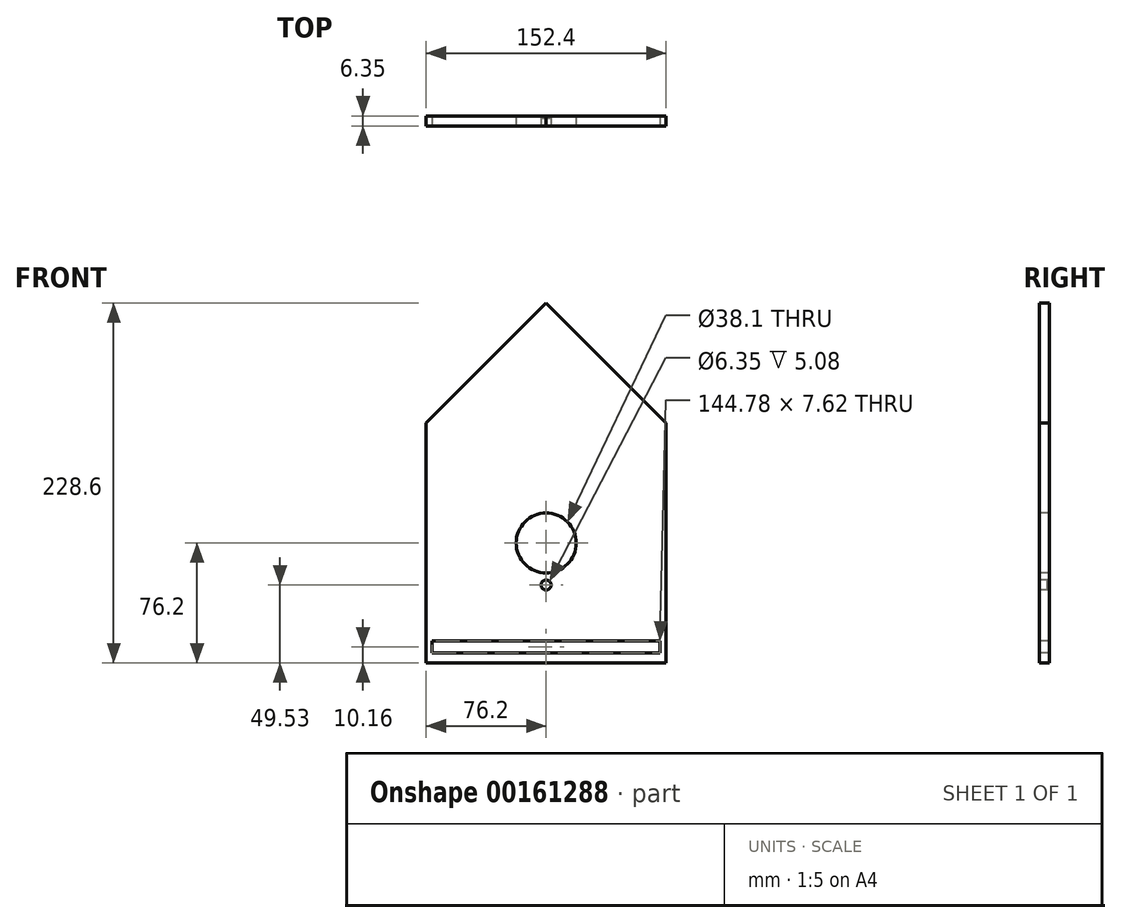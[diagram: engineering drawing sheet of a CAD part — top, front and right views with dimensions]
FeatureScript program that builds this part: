
annotation { "Feature Type Name" : "Feature", "Feature Type Description" : "" }
export const myFeature = defineFeature(function(context is Context, id is Id, definition is map)
    precondition{}
    {
        {
            var Q0;
            Q0=qCreatedBy(makeId("Front.planeOp"),FACE);
            var sketch = newSketch(context, id + "F0", { "sketchPlane" : qUnion([Q0])});
            skLineSegment(sketch, "E0.bottom", {"start": v(0, 0) * mm, "end": v(152.4, 0) * mm});
            skLineSegment(sketch, "E0.top", {"start": v(0, -152.4) * mm, "end": v(152.4, -152.4) * mm});
            skLineSegment(sketch, "E0.left", {"start": v(0, 0) * mm, "end": v(0, -152.4) * mm});
            skLineSegment(sketch, "E0.right", {"start": v(152.4, 0) * mm, "end": v(152.4, -152.4) * mm});
            skLineSegment(sketch, "E1", {"start": v(0, 0) * mm, "end": v(76.2, 76.2) * mm});
            skLineSegment(sketch, "E2", {"start": v(76.2, 76.2) * mm, "end": v(152.4, 0) * mm});
            skSolve(sketch);
        }
        {
            var Q0;
            Q0 = qSketchRegion(id + "F0", true);
            extrude(context, id + "F1", {"entities" : qUnion([Q0]), "depth" : 6.35 * mm});
        }
        {
            var Q0;
            Q0=makeQuery(id+"F1.opExtrude","CAP_FACE",FACE,{"disambiguationData":[OSD([sQuery(id+"F0.wireOp",EDGE,"E0.top"),sQuery(id+"F0.wireOp",EDGE,"E0.left"),sQuery(id+"F0.wireOp",EDGE,"E0.right"),sQuery(id+"F0.wireOp",EDGE,"E1"),sQuery(id+"F0.wireOp",EDGE,"E2")])],"isStart":false});
            var sketch = newSketch(context, id + "F2", { "sketchPlane" : qUnion([Q0])});
            skLineSegment(sketch, "E3", {"start": v(0, 0) * mm, "end": v(152.4, -152.4) * mm, "construction": true});
            skLineSegment(sketch, "E4", {"start": v(0, -152.4) * mm, "end": v(152.4, 0) * mm, "construction": true});
            skCircle(sketch, "E5", {"center": v(76.2, -76.2) * mm, "radius": 19.05 * mm});
            skSolve(sketch);
        }
        {
            var Q0;
            Q0=makeQuery(id+"F2.imprint","IMPRINT",FACE,{"disambiguationData":[TD([[makeQuery(id+"F2.imprint","IMPRINT",EDGE,{"derivedFrom":sQuery(id+"F2.wireOp",EDGE,"E5")}),1.0]])]});
            extrude(context, id + "F3", {"entities" : qUnion([Q0]), "operationType" : NewBodyOperationType.REMOVE, "endBound" : BoundingType.THROUGH_ALL, "oppositeDirection" : true, "depth" : 6.6 * mm});
        }
        {
            var Q0;
            Q0=makeQuery(id+"F1.opExtrude","CAP_FACE",FACE,{"disambiguationData":[OSD([sQuery(id+"F0.wireOp",EDGE,"E0.top"),sQuery(id+"F0.wireOp",EDGE,"E0.left"),sQuery(id+"F0.wireOp",EDGE,"E0.right"),sQuery(id+"F0.wireOp",EDGE,"E1"),sQuery(id+"F0.wireOp",EDGE,"E2")])],"isStart":false});
            var sketch = newSketch(context, id + "F4", { "sketchPlane" : qUnion([Q0])});
            skCircle(sketch, "E6", {"center": v(76.2, -102.87) * mm, "radius": 3.18 * mm});
            skPoint(sketch, "E6.centerSnap0", {"position": v(76.2, -152.4) * mm});
            skSolve(sketch);
        }
        {
            var Q0;
            Q0 = qSketchRegion(id + "F4", true);
            extrude(context, id + "F5", {"entities" : qUnion([Q0]), "operationType" : NewBodyOperationType.REMOVE, "oppositeDirection" : true, "depth" : 5.08 * mm});
        }
        {
            var Q0;
            Q0=makeQuery(id+"F1.opExtrude","CAP_FACE",FACE,{"disambiguationData":[OSD([sQuery(id+"F0.wireOp",EDGE,"E0.top"),sQuery(id+"F0.wireOp",EDGE,"E0.left"),sQuery(id+"F0.wireOp",EDGE,"E0.right"),sQuery(id+"F0.wireOp",EDGE,"E1"),sQuery(id+"F0.wireOp",EDGE,"E2")])],"isStart":false});
            var sketch = newSketch(context, id + "F6", { "sketchPlane" : qUnion([Q0])});
            skLineSegment(sketch, "E7.bottom", {"start": v(3.81, -146.05) * mm, "end": v(148.6, -146.05) * mm});
            skLineSegment(sketch, "E7.top", {"start": v(3.81, -138.43) * mm, "end": v(148.6, -138.43) * mm});
            skLineSegment(sketch, "E7.left", {"start": v(3.81, -146.05) * mm, "end": v(3.8, -138.43) * mm});
            skLineSegment(sketch, "E7.right", {"start": v(148.6, -146.05) * mm, "end": v(148.6, -138.43) * mm});
            skSolve(sketch);
        }
        {
            var Q0;
            Q0 = qSketchRegion(id + "F6", true);
            extrude(context, id + "F7", {"entities" : qUnion([Q0]), "operationType" : NewBodyOperationType.REMOVE, "oppositeDirection" : true, "depth" : 25.4 * mm});
        }
    });
